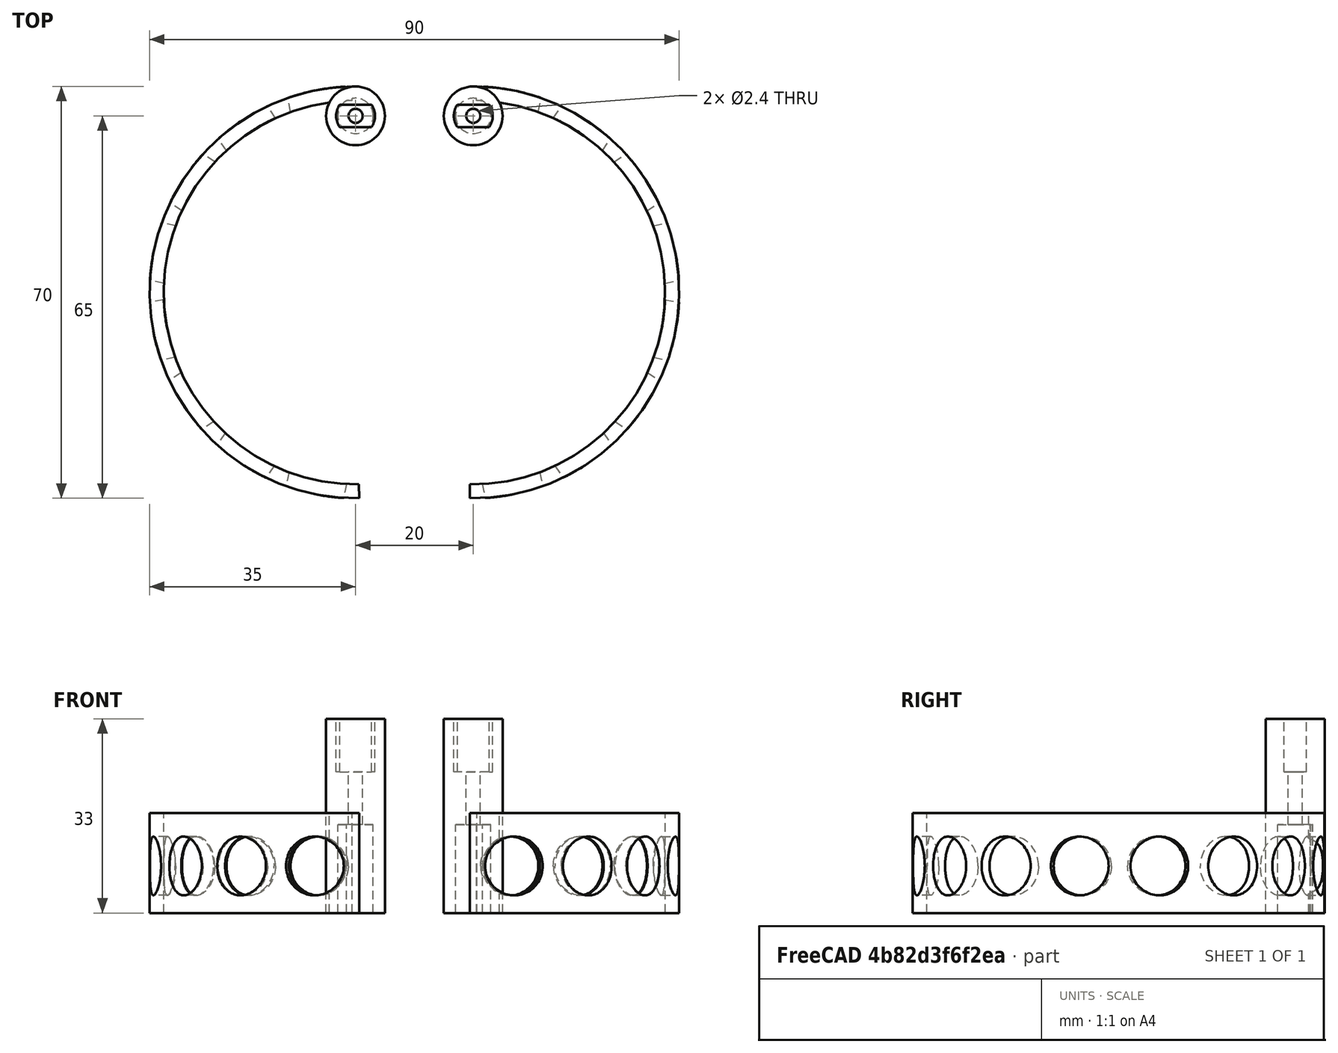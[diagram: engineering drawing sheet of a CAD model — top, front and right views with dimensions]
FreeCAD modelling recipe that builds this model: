
FCSTD DOCUMENT  (FreeCAD 0.15R4671 (Git))
Label: jpataModif1
License: CreativeCommons Attribution-ShareAlike
LicenseURL: http://creativecommons.org/licenses/by-sa/4.0/
objects: Part::Cylinder×7, Part::Cut×3, Part::MultiFuse×3, Part::Box×2, Part::MultiCommon×2, Part::FeaturePython×1, Part::Mirroring×1
note: 19 computed .brp shape members not serialized (recipe doc carries the construction recipe); baked Part::Feature solids carry a one-line shape summary decoded from their .brp

FEATURE [Part::Cylinder] Cylinder
  Angle = 360
  Height = 12
  Radius = 3.3
FEATURE [Part::Box] Box  label="Cube"
  Height = 9
  Length = 10
  Placement = pos=(-5,-1.9,3) rot=(0,0,1;0rad)
  Width = 3.8
FEATURE [Part::MultiCommon] Common
  Placement = pos=(0,0,21) rot=(0,0,1;0rad)
  Shapes = -> [Cylinder,Box]
FEATURE [Part::Cylinder] Cylinder001
  Angle = 360
  Height = 33
  Radius = 5
FEATURE [Part::Cylinder] Cylinder003
  Angle = 360
  Height = 17
  Radius = 35
FEATURE [Part::Cylinder] Cylinder004
  Angle = 360
  Height = 19
  Radius = 32.6
FEATURE [Part::Cut] Cut002
  Base = -> Cylinder003
  Tool = -> Cylinder004
FEATURE [Part::Cylinder] Cylinder005
  Angle = 360
  Height = 16
  Placement = pos=(23,0,8) rot=(0,1,0;1.5708rad)
  Radius = 5
FEATURE [Part::FeaturePython] Array  # Draft array (typed FeaturePython)
  Angle = 360
  ArrayType = 1
  Axis = (0,0,1)
  Base = -> Cylinder005
  Center = (0,0,0)
  Fuse = false
  IntervalAxis = (0,0,0)
  IntervalX = (1,0,0)
  IntervalY = (0,1,0)
  IntervalZ = (0,0,0)
  NumberPolar = 16
  NumberX = 2
  NumberY = 2
  NumberZ = 1
FEATURE [Part::Cut] Cut003
  Base = -> Cut002
  Tool = -> Array
FEATURE [Part::Box] Box003  label="Cube003"
  Height = 20
  Length = 106
  Placement = pos=(-7.64052,-43.3315,0) rot=(0,0,1;1.39626rad)
  Width = 45
FEATURE [Part::MultiCommon] Common001
  Placement = pos=(0,0,0) rot=(0,0,1;0.191986rad)
  Shapes = -> [Cut003,Box003]
FEATURE [Part::Cylinder] Cylinder006
  Angle = 360
  Height = 15
  Radius = 3
FEATURE [Part::Cylinder] Cylinder007
  Angle = 360
  Height = 10
  Placement = pos=(0,0,15) rot=(0,0,1;0rad)
  Radius = 1.2
FEATURE [Part::MultiFuse] Fusion
  Shapes = -> [Common,Cylinder006,Cylinder007]
FEATURE [Part::Cut] Cut
  Base = -> Cylinder001
  Placement = pos=(0,30,0) rot=(0,0,1;0rad)
  Tool = -> Fusion
FEATURE [Part::MultiFuse] Fusion001
  Shapes = -> [Common001,Cut]
FEATURE [Part::MultiFuse] Fusion002
  Shapes = -> [Common001,Cut]
FEATURE [Part::Mirroring] Part__Mirroring  label="Fusion002 (Mirror #1)"
  Base = (0,0,0)
  Normal = (1,0,0)
  Placement = pos=(20,0,0) rot=(0,0,1;0rad)
  Source = -> Fusion002
